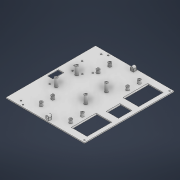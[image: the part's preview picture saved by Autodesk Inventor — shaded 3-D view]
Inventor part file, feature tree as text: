
AUTODESK INVENTOR PART (.ipt)
format: ipt  version: 2021 (Build 250183000, 183)  size: 551,424 bytes
history: native  units: mm
features: extrude x13, sketch x10, projected_geometry x8, fillet x4, other x1
ambient origin geometry x8: Origin, YZ Plane, XZ Plane, XY Plane, X Axis, Y Axis, Z Axis, Center Point
bodies: Volumenkörper1 (feature_tree)
feature tree (36):
  other  "Obenplatte_hinten"
  extrude  "Extrusion1"  Depth=200.0mm
  extrude  "Extrusion2"  Depth=2.0mm
  extrude  "Extrusion4"  Depth=5.0mm
  extrude  "Extrusion5"  Depth=2.0mm TaperAngle=0.0deg
  fillet  "Rundung1"  Radius=3.2mm
  fillet  "Rundung2"  Radius=23.0mm
  sketch  "Skizze5"  dims[d28=10.5mm d29=3.2mm]
  extrude  "Extrusion6"  Depth=3.2mm
  extrude  "Extrusion8"  Depth=74.5mm
  fillet  "Rundung3"  Radius=3.2mm
  extrude  "Extrusion9"  Depth=74.5mm
  extrude  "Extrusion7"  Depth=10.5mm
  extrude  "Extrusion10"  Depth=10.0mm TaperAngle=0.0deg
  extrude  "Extrusion11"  Depth=5.0mm
  extrude  "Extrusion12"  Depth=10.0mm
  extrude  "Extrusion13"  Depth=24.0mm
  extrude  "Extrusion14"  Depth=5.0mm
  fillet  "Rundung4"  Radius=88.0mm
  sketch  "Skizze1"  dims[d0=175.0mm d1=200.0mm]
  sketch  "Skizze2"  dims[d2=2.0mm d3=0.0mm d4=3.2mm]
  sketch  "Skizze3"  dims[d6=5.0mm d7=3.2mm]
  sketch  "Skizze4"  dims[d9=5.0mm d10=2.0mm d11=0.0mm d26=3.2mm d27=23.0mm]
  sketch  "Skizze6"  dims[d30=23.0mm d31=74.5mm d32=3.2mm]
  projected_geometry  "Projizierte Kontur1"
  projected_geometry  "Projizierte Kontur2"
  projected_geometry  "Projizierte Kontur3"
  projected_geometry  "Projizierte Kontur4"
  sketch  "Skizze8"  dims[d33=23.0mm d34=74.5mm]
  projected_geometry  "Projizierte Kontur5"
  projected_geometry  "Projizierte Kontur6"
  projected_geometry  "Projizierte Kontur7"
  projected_geometry  "Projizierte Kontur8"
  sketch  "Skizze10"  dims[d35=3.2mm d36=10.5mm]
  sketch  "Skizze11"  dims[d37=23.0mm d38=10.0mm d39=0.0mm]
  sketch  "Skizze12"  dims[d40=33.0mm d41=5.0mm d42=10.0mm d43=24.0mm d44=5.0mm d45=88.0mm d46=10.0mm d47=0.0mm d48=2.0mm d49=2.0mm d50=7.0mm d51=7.0mm d52=7.0mm d53=7.0mm d54=23.5mm d55=23.5mm d56=55.0mm d57=66.0mm d58=55.0mm d59=66.0mm d60=26.0mm d61=26.0mm d62=33.0mm d63=12.0mm d64=15.0mm d65=55.0mm d66=7.0mm d67=0.0mm d68=4.0mm d69=4.0mm d70=4.0mm d71=4.0mm d72=4.0mm d73=4.0mm d74=4.0mm d75=4.0mm d76=5.0mm d77=0.0mm d78=5.0mm d79=0.0mm d80=2.0mm d81=7.0mm d82=7.0mm d83=7.0mm d84=7.0mm d85=35.0mm d86=35.0mm d87=46.0mm d88=46.0mm d89=23.0mm d90=23.0mm d91=66.0mm d92=66.0mm d93=25.0mm d94=30.0mm d95=9.0mm d96=18.0mm d97=0.0mm d98=4.0mm d99=4.0mm d100=4.0mm d101=4.0mm d102=5.0mm d103=0.0mm d104=3.2mm d105=3.2mm d106=13.8mm d107=0.2mm d108=6.8mm d109=3.2mm d110=3.2mm d111=15.0mm d112=15.0mm d113=17.0mm d115=10.0mm d116=0.0mm d117=7.0mm d118=7.0mm d119=2.2mm d120=81.5mm d121=9.0mm d122=0.0mm d123=4.0mm d124=5.0mm d125=3.5mm d126=5.0mm d127=0.0mm d128=4.0mm d129=5.0mm d130=3.5mm d131=5.0mm d132=0.0mm d133=3.5mm d134=55.897306mm d135=49.854048mm d136=40.145952mm d137=45.0mm d138=1.5mm d139=1.5mm]
